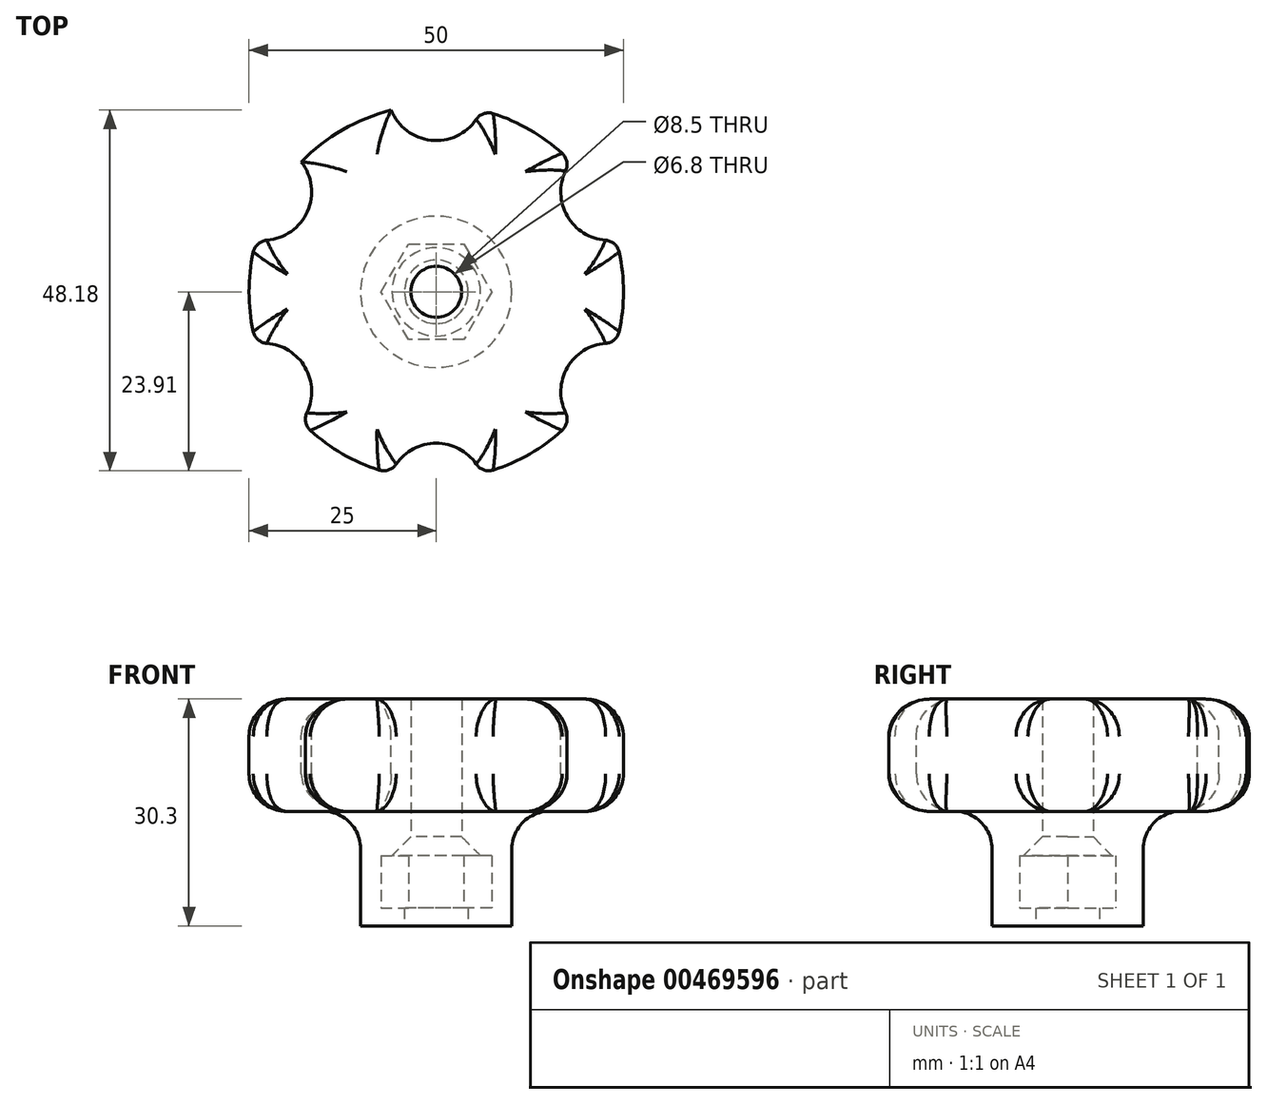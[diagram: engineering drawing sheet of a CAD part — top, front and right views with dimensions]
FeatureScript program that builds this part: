
annotation { "Feature Type Name" : "Feature", "Feature Type Description" : "" }
export const myFeature = defineFeature(function(context is Context, id is Id, definition is map)
    precondition{}
    {
        {
            var Q0;
            Q0=qCreatedBy(makeId("Top.planeOp"),FACE);
            var sketch = newSketch(context, id + "F0", { "sketchPlane" : qUnion([Q0])});
            skLineSegment(sketch, "E0.0", {"start": v(-7.4, 0) * mm, "end": v(-3.7, 6.4) * mm});
            skLineSegment(sketch, "E0.1", {"start": v(-3.7, 6.4) * mm, "end": v(3.7, 6.4) * mm});
            skLineSegment(sketch, "E0.2", {"start": v(3.7, 6.4) * mm, "end": v(7.4, 0) * mm});
            skLineSegment(sketch, "E0.3", {"start": v(7.4, 0) * mm, "end": v(3.7, -6.4) * mm});
            skLineSegment(sketch, "E0.4", {"start": v(3.7, -6.4) * mm, "end": v(-3.7, -6.4) * mm});
            skLineSegment(sketch, "E0.5", {"start": v(-3.7, -6.4) * mm, "end": v(-7.4, 0) * mm});
            skPoint(sketch, "E1.center.orphan", {"position": v(0, 0) * mm});
            skSolve(sketch);
        }
        {
            var Q0;
            Q0=makeQuery(id+"F0.imprint","IMPRINT",FACE,{"disambiguationData":[TD([[makeQuery(id+"F0.imprint","IMPRINT",EDGE,{"derivedFrom":sQuery(id+"F0.wireOp",EDGE,"E0.0")}),-1.0]])]});
            extrude(context, id + "F1", {"entities" : qUnion([Q0]), "depth" : 7 * mm});
        }
        {
            var Q0;
            Q0=qCreatedBy(makeId("Front.planeOp"),FACE);
            var sketch = newSketch(context, id + "F2", { "sketchPlane" : qUnion([Q0])});
            skLineSegment(sketch, "E2", {"start": v(-10.1, -2.4) * mm, "end": v(-10.1, 7.9) * mm});
            skLineSegment(sketch, "E3", {"start": v(-15.1, 12.9) * mm, "end": v(-25, 12.9) * mm});
            skLineSegment(sketch, "E4", {"start": v(-25, 12.9) * mm, "end": v(-25, 27.9) * mm});
            skLineSegment(sketch, "E5", {"start": v(-25, 27.9) * mm, "end": v(-3.4, 27.9) * mm});
            skLineSegment(sketch, "E6", {"start": v(-3.4, 27.9) * mm, "end": v(-3.4, 0) * mm});
            skLineSegment(sketch, "E7", {"start": v(-3.4, 0) * mm, "end": v(-4.25, 0) * mm});
            skLineSegment(sketch, "E8", {"start": v(-4.25, 0) * mm, "end": v(-4.25, -2.4) * mm});
            skLineSegment(sketch, "E9", {"start": v(-4.25, -2.4) * mm, "end": v(-10.1, -2.4) * mm});
            skLineSegment(sketch, "E10", {"start": v(0, 0) * mm, "end": v(0, 19.48) * mm});
            skPoint(sketch, "E11.visualSharp", {"position": v(-10.1, 12.9) * mm});
            skArc(sketch, "E11.filletArc", {"start": v(-10.1, 7.9) * mm, "mid": v(-11.56, 11.44) * mm, "end": v(-15.1, 12.9) * mm});
            skSolve(sketch);
        }
        {
            var Q0;
            Q0=makeQuery(id+"F2.imprint","IMPRINT",FACE,{"disambiguationData":[TD([[makeQuery(id+"F2.imprint","IMPRINT",EDGE,{"derivedFrom":sQuery(id+"F2.wireOp",EDGE,"E2")}),-1.0]])]});
            var Q1;
            Q1=sQuery(id+"F2.wireOp",EDGE,"E10");
            revolve(context, id + "F3", {"entities" : qUnion([Q0]), "axis" : qUnion([Q1]), "revolveType" : RevolveType.FULL});
        }
        {
            var Q0;
            Q0=makeQuery(id+"F3.opRevolve","SWEPT_FACE",FACE,{"disambiguationData":[OSD([sQuery(id+"F2.wireOp",EDGE,"E5")])]});
            var sketch = newSketch(context, id + "F4", { "sketchPlane" : qUnion([Q0])});
            skPoint(sketch, "E12.cCircle.center.orphan", {"position": v(0, 0) * mm});
            skArc(sketch, "E13", {"start": v(-24.02, 6.93) * mm, "mid": v(-25, 0) * mm, "end": v(-24.02, -6.93) * mm});
            skArc(sketch, "E14", {"start": v(-24.02, 6.93) * mm, "mid": v(-17.5, 10.1) * mm, "end": v(-18.01, 17.34) * mm});
            skArc(sketch, "E15", {"start": v(-6, 24.27) * mm, "mid": v(0, 20.21) * mm, "end": v(6, 24.27) * mm});
            skArc(sketch, "E16", {"start": v(18.01, 17.34) * mm, "mid": v(17.5, 10.1) * mm, "end": v(24.02, 6.93) * mm});
            skArc(sketch, "E17", {"start": v(24.02, -6.93) * mm, "mid": v(17.5, -10.1) * mm, "end": v(18.01, -17.34) * mm});
            skArc(sketch, "E18", {"start": v(6, -24.27) * mm, "mid": v(0, -20.21) * mm, "end": v(-6, -24.27) * mm});
            skArc(sketch, "E19", {"start": v(-18.01, -17.34) * mm, "mid": v(-17.5, -10.1) * mm, "end": v(-24.02, -6.93) * mm});
            skArc(sketch, "E20.trimOffspring", {"start": v(-6, 24.27) * mm, "mid": v(-12.5, 21.65) * mm, "end": v(-18.01, 17.34) * mm});
            skArc(sketch, "E21.trimOffspring", {"start": v(18.01, 17.34) * mm, "mid": v(12.5, 21.65) * mm, "end": v(6, 24.27) * mm});
            skArc(sketch, "E22.trimOffspring", {"start": v(6, -24.27) * mm, "mid": v(12.5, -21.65) * mm, "end": v(18.01, -17.34) * mm});
            skArc(sketch, "E23.trimOffspring", {"start": v(24.02, -6.93) * mm, "mid": v(25, 0) * mm, "end": v(24.02, 6.93) * mm});
            skPoint(sketch, "E24.start.orphan", {"position": v(-25, 0) * mm});
            skArc(sketch, "E25.trimOffspring", {"start": v(-18.01, -17.34) * mm, "mid": v(-12.5, -21.65) * mm, "end": v(-6, -24.27) * mm});
            skSolve(sketch);
        }
        {
            var Q0;
            Q0 = qSketchRegion(id + "F4", true);
            extrude(context, id + "F5", {"entities" : qUnion([Q0]), "endBound" : BoundingType.SYMMETRIC, "oppositeDirection" : true, "depth" : 86.2 * mm});
        }
        {
            var Q0;
            Q0=makeQuery(id+"F3.opRevolve","SWEPT_BODY",BODY,{"disambiguationData":[OSD([sQuery(id+"F2.wireOp",EDGE,"E2"),sQuery(id+"F2.wireOp",EDGE,"E3"),sQuery(id+"F2.wireOp",EDGE,"E4"),sQuery(id+"F2.wireOp",EDGE,"E5"),sQuery(id+"F2.wireOp",EDGE,"E6"),sQuery(id+"F2.wireOp",EDGE,"E7"),sQuery(id+"F2.wireOp",EDGE,"E8"),sQuery(id+"F2.wireOp",EDGE,"E9")])]});
            var Q1;
            Q1=makeQuery(id+"F5.opExtrude","SWEPT_BODY",BODY,{"disambiguationData":[OSD([sQuery(id+"F4.wireOp",EDGE,"E13"),sQuery(id+"F4.wireOp",EDGE,"E14"),sQuery(id+"F4.wireOp",EDGE,"E15"),sQuery(id+"F4.wireOp",EDGE,"E16"),sQuery(id+"F4.wireOp",EDGE,"E17"),sQuery(id+"F4.wireOp",EDGE,"E18"),sQuery(id+"F4.wireOp",EDGE,"E19"),sQuery(id+"F4.wireOp",EDGE,"E20.trimOffspring"),sQuery(id+"F4.wireOp",EDGE,"E21.trimOffspring"),sQuery(id+"F4.wireOp",EDGE,"E22.trimOffspring"),sQuery(id+"F4.wireOp",EDGE,"E23.trimOffspring"),sQuery(id+"F4.wireOp",EDGE,"E25.trimOffspring")])]});
            booleanBodies(context, id + "F6", {"operationType" : BooleanOperationType.INTERSECTION, "tools" : qUnion([Q0, Q1])});
        }
        {
            var Q0;
            Q0=makeQuery(id+"F6.opBoolean","INTERSECT",EDGE,{"derivedFrom":[makeQuery(id+"F3.opRevolve","SWEPT_FACE",FACE,{"disambiguationData":[OSD([sQuery(id+"F2.wireOp",EDGE,"E5")])]}),makeQuery(id+"F5.opExtrude","SWEPT_FACE",FACE,{"disambiguationData":[OSD([sQuery(id+"F4.wireOp",EDGE,"E16")])]})]});
            var Q1;
            {var subQ0=sQuery(id+"F2.wireOp",EDGE,"E4");var subQ1=sQuery(id+"F2.wireOp",EDGE,"E5");Q1=makeQuery(id+"F6.opBoolean","SPLIT",EDGE,{"disambiguationData":[TD([makeQuery(id+"F3.opRevolve","SWEPT_FACE",FACE,{"disambiguationData":[OSD([subQ0])]}),makeQuery(id+"F3.opRevolve","SWEPT_FACE",FACE,{"disambiguationData":[OSD([subQ1])]}),makeQuery(id+"F5.opExtrude","SWEPT_FACE",FACE,{"disambiguationData":[OSD([sQuery(id+"F4.wireOp",EDGE,"E15")])]}),makeQuery(id+"F5.opExtrude","SWEPT_FACE",FACE,{"disambiguationData":[OSD([sQuery(id+"F4.wireOp",EDGE,"E16")])]})])],"derivedFrom":makeQuery(id+"F3.opRevolve","SWEPT_EDGE",EDGE,{"disambiguationData":[OSD([subQ0,subQ1])]})});}
            var Q2;
            Q2=makeQuery(id+"F6.opBoolean","INTERSECT",EDGE,{"derivedFrom":[makeQuery(id+"F3.opRevolve","SWEPT_FACE",FACE,{"disambiguationData":[OSD([sQuery(id+"F2.wireOp",EDGE,"E5")])]}),makeQuery(id+"F5.opExtrude","SWEPT_FACE",FACE,{"disambiguationData":[OSD([sQuery(id+"F4.wireOp",EDGE,"E15")])]})]});
            var Q3;
            Q3=makeQuery(id+"F6.opBoolean","INTERSECT",EDGE,{"derivedFrom":[makeQuery(id+"F3.opRevolve","SWEPT_FACE",FACE,{"disambiguationData":[OSD([sQuery(id+"F2.wireOp",EDGE,"E5")])]}),makeQuery(id+"F5.opExtrude","SWEPT_FACE",FACE,{"disambiguationData":[OSD([sQuery(id+"F4.wireOp",EDGE,"E17")])]})]});
            var Q4;
            {var subQ0=sQuery(id+"F2.wireOp",EDGE,"E4");var subQ1=sQuery(id+"F2.wireOp",EDGE,"E5");Q4=makeQuery(id+"F6.opBoolean","SPLIT",EDGE,{"disambiguationData":[TD([makeQuery(id+"F3.opRevolve","SWEPT_FACE",FACE,{"disambiguationData":[OSD([subQ0])]}),makeQuery(id+"F3.opRevolve","SWEPT_FACE",FACE,{"disambiguationData":[OSD([subQ1])]}),makeQuery(id+"F5.opExtrude","SWEPT_FACE",FACE,{"disambiguationData":[OSD([sQuery(id+"F4.wireOp",EDGE,"E16")])]}),makeQuery(id+"F5.opExtrude","SWEPT_FACE",FACE,{"disambiguationData":[OSD([sQuery(id+"F4.wireOp",EDGE,"E17")])]})])],"derivedFrom":makeQuery(id+"F3.opRevolve","SWEPT_EDGE",EDGE,{"disambiguationData":[OSD([subQ0,subQ1])]})});}
            var Q5;
            Q5=makeQuery(id+"F6.opBoolean","INTERSECT",EDGE,{"derivedFrom":[makeQuery(id+"F3.opRevolve","SWEPT_FACE",FACE,{"disambiguationData":[OSD([sQuery(id+"F2.wireOp",EDGE,"E5")])]}),makeQuery(id+"F5.opExtrude","SWEPT_FACE",FACE,{"disambiguationData":[OSD([sQuery(id+"F4.wireOp",EDGE,"E14")])]})]});
            var Q6;
            Q6=makeQuery(id+"F6.opBoolean","INTERSECT",EDGE,{"derivedFrom":[makeQuery(id+"F3.opRevolve","SWEPT_FACE",FACE,{"disambiguationData":[OSD([sQuery(id+"F2.wireOp",EDGE,"E5")])]}),makeQuery(id+"F5.opExtrude","SWEPT_FACE",FACE,{"disambiguationData":[OSD([sQuery(id+"F4.wireOp",EDGE,"E19")])]})]});
            var Q7;
            {var subQ0=sQuery(id+"F2.wireOp",EDGE,"E4");var subQ1=sQuery(id+"F2.wireOp",EDGE,"E5");Q7=makeQuery(id+"F6.opBoolean","SPLIT",EDGE,{"disambiguationData":[TD([makeQuery(id+"F3.opRevolve","SWEPT_FACE",FACE,{"disambiguationData":[OSD([subQ0])]}),makeQuery(id+"F3.opRevolve","SWEPT_FACE",FACE,{"disambiguationData":[OSD([subQ1])]}),makeQuery(id+"F5.opExtrude","SWEPT_FACE",FACE,{"disambiguationData":[OSD([sQuery(id+"F4.wireOp",EDGE,"E14")])]}),makeQuery(id+"F5.opExtrude","SWEPT_FACE",FACE,{"disambiguationData":[OSD([sQuery(id+"F4.wireOp",EDGE,"E19")])]})])],"derivedFrom":makeQuery(id+"F3.opRevolve","SWEPT_EDGE",EDGE,{"disambiguationData":[OSD([subQ0,subQ1])]})});}
            var Q8;
            {var subQ0=sQuery(id+"F2.wireOp",EDGE,"E4");var subQ1=sQuery(id+"F2.wireOp",EDGE,"E5");Q8=makeQuery(id+"F6.opBoolean","SPLIT",EDGE,{"disambiguationData":[TD([makeQuery(id+"F3.opRevolve","SWEPT_FACE",FACE,{"disambiguationData":[OSD([subQ0])]}),makeQuery(id+"F3.opRevolve","SWEPT_FACE",FACE,{"disambiguationData":[OSD([subQ1])]}),makeQuery(id+"F5.opExtrude","SWEPT_FACE",FACE,{"disambiguationData":[OSD([sQuery(id+"F4.wireOp",EDGE,"E14")])]}),makeQuery(id+"F5.opExtrude","SWEPT_FACE",FACE,{"disambiguationData":[OSD([sQuery(id+"F4.wireOp",EDGE,"E15")])]})])],"derivedFrom":makeQuery(id+"F3.opRevolve","SWEPT_EDGE",EDGE,{"disambiguationData":[OSD([subQ0,subQ1])]})});}
            var Q9;
            Q9=makeQuery(id+"F6.opBoolean","INTERSECT",EDGE,{"derivedFrom":[makeQuery(id+"F3.opRevolve","SWEPT_FACE",FACE,{"disambiguationData":[OSD([sQuery(id+"F2.wireOp",EDGE,"E5")])]}),makeQuery(id+"F5.opExtrude","SWEPT_FACE",FACE,{"disambiguationData":[OSD([sQuery(id+"F4.wireOp",EDGE,"E18")])]})]});
            var Q10;
            {var subQ0=sQuery(id+"F2.wireOp",EDGE,"E4");var subQ1=sQuery(id+"F2.wireOp",EDGE,"E5");Q10=makeQuery(id+"F6.opBoolean","SPLIT",EDGE,{"disambiguationData":[TD([makeQuery(id+"F3.opRevolve","SWEPT_FACE",FACE,{"disambiguationData":[OSD([subQ0])]}),makeQuery(id+"F3.opRevolve","SWEPT_FACE",FACE,{"disambiguationData":[OSD([subQ1])]}),makeQuery(id+"F5.opExtrude","SWEPT_FACE",FACE,{"disambiguationData":[OSD([sQuery(id+"F4.wireOp",EDGE,"E18")])]}),makeQuery(id+"F5.opExtrude","SWEPT_FACE",FACE,{"disambiguationData":[OSD([sQuery(id+"F4.wireOp",EDGE,"E19")])]})])],"derivedFrom":makeQuery(id+"F3.opRevolve","SWEPT_EDGE",EDGE,{"disambiguationData":[OSD([subQ0,subQ1])]})});}
            var Q11;
            {var subQ0=sQuery(id+"F2.wireOp",EDGE,"E4");var subQ1=sQuery(id+"F2.wireOp",EDGE,"E5");Q11=makeQuery(id+"F6.opBoolean","SPLIT",EDGE,{"disambiguationData":[TD([makeQuery(id+"F3.opRevolve","SWEPT_FACE",FACE,{"disambiguationData":[OSD([subQ0])]}),makeQuery(id+"F3.opRevolve","SWEPT_FACE",FACE,{"disambiguationData":[OSD([subQ1])]}),makeQuery(id+"F5.opExtrude","SWEPT_FACE",FACE,{"disambiguationData":[OSD([sQuery(id+"F4.wireOp",EDGE,"E17")])]}),makeQuery(id+"F5.opExtrude","SWEPT_FACE",FACE,{"disambiguationData":[OSD([sQuery(id+"F4.wireOp",EDGE,"E18")])]})])],"derivedFrom":makeQuery(id+"F3.opRevolve","SWEPT_EDGE",EDGE,{"disambiguationData":[OSD([subQ0,subQ1])]})});}
            fillet(context, id + "F7", {"entities" : qUnion([Q0, Q1, Q2, Q3, Q4, Q5, Q6, Q7, Q8, Q9, Q10, Q11]), "radius" : 5 * mm, "tangentPropagation" : true, "allowEdgeOverflow" : false});
        }
        {
            var Q0;
            Q0=makeQuery(id+"F6.opBoolean","INTERSECT",EDGE,{"derivedFrom":[makeQuery(id+"F3.opRevolve","SWEPT_FACE",FACE,{"disambiguationData":[OSD([sQuery(id+"F2.wireOp",EDGE,"E3")])]}),makeQuery(id+"F5.opExtrude","SWEPT_FACE",FACE,{"disambiguationData":[OSD([sQuery(id+"F4.wireOp",EDGE,"E18")])]})]});
            var Q1;
            Q1=makeQuery(id+"F6.opBoolean","INTERSECT",EDGE,{"derivedFrom":[makeQuery(id+"F3.opRevolve","SWEPT_FACE",FACE,{"disambiguationData":[OSD([sQuery(id+"F2.wireOp",EDGE,"E3")])]}),makeQuery(id+"F5.opExtrude","SWEPT_FACE",FACE,{"disambiguationData":[OSD([sQuery(id+"F4.wireOp",EDGE,"E17")])]})]});
            var Q2;
            Q2=makeQuery(id+"F6.opBoolean","INTERSECT",EDGE,{"derivedFrom":[makeQuery(id+"F3.opRevolve","SWEPT_FACE",FACE,{"disambiguationData":[OSD([sQuery(id+"F2.wireOp",EDGE,"E3")])]}),makeQuery(id+"F5.opExtrude","SWEPT_FACE",FACE,{"disambiguationData":[OSD([sQuery(id+"F4.wireOp",EDGE,"E19")])]})]});
            var Q3;
            {var subQ0=sQuery(id+"F2.wireOp",EDGE,"E3");var subQ1=sQuery(id+"F2.wireOp",EDGE,"E4");Q3=makeQuery(id+"F6.opBoolean","SPLIT",EDGE,{"disambiguationData":[TD([makeQuery(id+"F3.opRevolve","SWEPT_FACE",FACE,{"disambiguationData":[OSD([subQ0])]}),makeQuery(id+"F3.opRevolve","SWEPT_FACE",FACE,{"disambiguationData":[OSD([subQ1])]}),makeQuery(id+"F5.opExtrude","SWEPT_FACE",FACE,{"disambiguationData":[OSD([sQuery(id+"F4.wireOp",EDGE,"E18")])]}),makeQuery(id+"F5.opExtrude","SWEPT_FACE",FACE,{"disambiguationData":[OSD([sQuery(id+"F4.wireOp",EDGE,"E19")])]})])],"derivedFrom":makeQuery(id+"F3.opRevolve","SWEPT_EDGE",EDGE,{"disambiguationData":[OSD([subQ0,subQ1])]})});}
            var Q4;
            {var subQ0=sQuery(id+"F2.wireOp",EDGE,"E3");var subQ1=sQuery(id+"F2.wireOp",EDGE,"E4");Q4=makeQuery(id+"F6.opBoolean","SPLIT",EDGE,{"disambiguationData":[TD([makeQuery(id+"F3.opRevolve","SWEPT_FACE",FACE,{"disambiguationData":[OSD([subQ0])]}),makeQuery(id+"F3.opRevolve","SWEPT_FACE",FACE,{"disambiguationData":[OSD([subQ1])]}),makeQuery(id+"F5.opExtrude","SWEPT_FACE",FACE,{"disambiguationData":[OSD([sQuery(id+"F4.wireOp",EDGE,"E17")])]}),makeQuery(id+"F5.opExtrude","SWEPT_FACE",FACE,{"disambiguationData":[OSD([sQuery(id+"F4.wireOp",EDGE,"E18")])]})])],"derivedFrom":makeQuery(id+"F3.opRevolve","SWEPT_EDGE",EDGE,{"disambiguationData":[OSD([subQ0,subQ1])]})});}
            var Q5;
            Q5=makeQuery(id+"F6.opBoolean","INTERSECT",EDGE,{"derivedFrom":[makeQuery(id+"F3.opRevolve","SWEPT_FACE",FACE,{"disambiguationData":[OSD([sQuery(id+"F2.wireOp",EDGE,"E3")])]}),makeQuery(id+"F5.opExtrude","SWEPT_FACE",FACE,{"disambiguationData":[OSD([sQuery(id+"F4.wireOp",EDGE,"E16")])]})]});
            var Q6;
            Q6=makeQuery(id+"F6.opBoolean","INTERSECT",EDGE,{"derivedFrom":[makeQuery(id+"F3.opRevolve","SWEPT_FACE",FACE,{"disambiguationData":[OSD([sQuery(id+"F2.wireOp",EDGE,"E3")])]}),makeQuery(id+"F5.opExtrude","SWEPT_FACE",FACE,{"disambiguationData":[OSD([sQuery(id+"F4.wireOp",EDGE,"E15")])]})]});
            var Q7;
            Q7=makeQuery(id+"F6.opBoolean","INTERSECT",EDGE,{"derivedFrom":[makeQuery(id+"F3.opRevolve","SWEPT_FACE",FACE,{"disambiguationData":[OSD([sQuery(id+"F2.wireOp",EDGE,"E3")])]}),makeQuery(id+"F5.opExtrude","SWEPT_FACE",FACE,{"disambiguationData":[OSD([sQuery(id+"F4.wireOp",EDGE,"E14")])]})]});
            var Q8;
            {var subQ0=sQuery(id+"F2.wireOp",EDGE,"E3");var subQ1=sQuery(id+"F2.wireOp",EDGE,"E4");Q8=makeQuery(id+"F6.opBoolean","SPLIT",EDGE,{"disambiguationData":[TD([makeQuery(id+"F3.opRevolve","SWEPT_FACE",FACE,{"disambiguationData":[OSD([subQ0])]}),makeQuery(id+"F3.opRevolve","SWEPT_FACE",FACE,{"disambiguationData":[OSD([subQ1])]}),makeQuery(id+"F5.opExtrude","SWEPT_FACE",FACE,{"disambiguationData":[OSD([sQuery(id+"F4.wireOp",EDGE,"E16")])]}),makeQuery(id+"F5.opExtrude","SWEPT_FACE",FACE,{"disambiguationData":[OSD([sQuery(id+"F4.wireOp",EDGE,"E17")])]})])],"derivedFrom":makeQuery(id+"F3.opRevolve","SWEPT_EDGE",EDGE,{"disambiguationData":[OSD([subQ0,subQ1])]})});}
            var Q9;
            {var subQ0=sQuery(id+"F2.wireOp",EDGE,"E3");var subQ1=sQuery(id+"F2.wireOp",EDGE,"E4");Q9=makeQuery(id+"F6.opBoolean","SPLIT",EDGE,{"disambiguationData":[TD([makeQuery(id+"F3.opRevolve","SWEPT_FACE",FACE,{"disambiguationData":[OSD([subQ0])]}),makeQuery(id+"F3.opRevolve","SWEPT_FACE",FACE,{"disambiguationData":[OSD([subQ1])]}),makeQuery(id+"F5.opExtrude","SWEPT_FACE",FACE,{"disambiguationData":[OSD([sQuery(id+"F4.wireOp",EDGE,"E15")])]}),makeQuery(id+"F5.opExtrude","SWEPT_FACE",FACE,{"disambiguationData":[OSD([sQuery(id+"F4.wireOp",EDGE,"E16")])]})])],"derivedFrom":makeQuery(id+"F3.opRevolve","SWEPT_EDGE",EDGE,{"disambiguationData":[OSD([subQ0,subQ1])]})});}
            var Q10;
            {var subQ0=sQuery(id+"F2.wireOp",EDGE,"E3");var subQ1=sQuery(id+"F2.wireOp",EDGE,"E4");Q10=makeQuery(id+"F6.opBoolean","SPLIT",EDGE,{"disambiguationData":[TD([makeQuery(id+"F3.opRevolve","SWEPT_FACE",FACE,{"disambiguationData":[OSD([subQ0])]}),makeQuery(id+"F3.opRevolve","SWEPT_FACE",FACE,{"disambiguationData":[OSD([subQ1])]}),makeQuery(id+"F5.opExtrude","SWEPT_FACE",FACE,{"disambiguationData":[OSD([sQuery(id+"F4.wireOp",EDGE,"E14")])]}),makeQuery(id+"F5.opExtrude","SWEPT_FACE",FACE,{"disambiguationData":[OSD([sQuery(id+"F4.wireOp",EDGE,"E15")])]})])],"derivedFrom":makeQuery(id+"F3.opRevolve","SWEPT_EDGE",EDGE,{"disambiguationData":[OSD([subQ0,subQ1])]})});}
            var Q11;
            {var subQ0=sQuery(id+"F2.wireOp",EDGE,"E3");var subQ1=sQuery(id+"F2.wireOp",EDGE,"E4");Q11=makeQuery(id+"F6.opBoolean","SPLIT",EDGE,{"disambiguationData":[TD([makeQuery(id+"F3.opRevolve","SWEPT_FACE",FACE,{"disambiguationData":[OSD([subQ0])]}),makeQuery(id+"F3.opRevolve","SWEPT_FACE",FACE,{"disambiguationData":[OSD([subQ1])]}),makeQuery(id+"F5.opExtrude","SWEPT_FACE",FACE,{"disambiguationData":[OSD([sQuery(id+"F4.wireOp",EDGE,"E14")])]}),makeQuery(id+"F5.opExtrude","SWEPT_FACE",FACE,{"disambiguationData":[OSD([sQuery(id+"F4.wireOp",EDGE,"E19")])]})])],"derivedFrom":makeQuery(id+"F3.opRevolve","SWEPT_EDGE",EDGE,{"disambiguationData":[OSD([subQ0,subQ1])]})});}
            fillet(context, id + "F8", {"entities" : qUnion([Q0, Q1, Q2, Q3, Q4, Q5, Q6, Q7, Q8, Q9, Q10, Q11]), "radius" : 5 * mm, "tangentPropagation" : true, "allowEdgeOverflow" : false});
        }
        {
            var Q0;
            Q0=makeQuery(id+"F5.opExtrude","SWEPT_EDGE",EDGE,{"disambiguationData":[OSD([sQuery(id+"F2.wireOp",EDGE,"E4"),sQuery(id+"F2.wireOp",EDGE,"E5"),sQuery(id+"F4.wireOp",EDGE,"E15"),sQuery(id+"F4.wireOp",EDGE,"E20.trimOffspring")])]});
            var Q1;
            Q1=makeQuery(id+"F5.opExtrude","SWEPT_EDGE",EDGE,{"disambiguationData":[OSD([sQuery(id+"F2.wireOp",EDGE,"E4"),sQuery(id+"F2.wireOp",EDGE,"E5"),sQuery(id+"F4.wireOp",EDGE,"E15"),sQuery(id+"F4.wireOp",EDGE,"E21.trimOffspring")])]});
            var Q2;
            Q2=makeQuery(id+"F5.opExtrude","SWEPT_EDGE",EDGE,{"disambiguationData":[OSD([sQuery(id+"F2.wireOp",EDGE,"E4"),sQuery(id+"F2.wireOp",EDGE,"E5"),sQuery(id+"F4.wireOp",EDGE,"E16"),sQuery(id+"F4.wireOp",EDGE,"E21.trimOffspring")])]});
            var Q3;
            Q3=makeQuery(id+"F5.opExtrude","SWEPT_EDGE",EDGE,{"disambiguationData":[OSD([sQuery(id+"F2.wireOp",EDGE,"E4"),sQuery(id+"F2.wireOp",EDGE,"E5"),sQuery(id+"F4.wireOp",EDGE,"E14"),sQuery(id+"F4.wireOp",EDGE,"E20.trimOffspring")])]});
            var Q4;
            Q4=makeQuery(id+"F5.opExtrude","SWEPT_EDGE",EDGE,{"disambiguationData":[OSD([sQuery(id+"F2.wireOp",EDGE,"E4"),sQuery(id+"F2.wireOp",EDGE,"E5"),sQuery(id+"F4.wireOp",EDGE,"E13"),sQuery(id+"F4.wireOp",EDGE,"E14")])]});
            var Q5;
            Q5=makeQuery(id+"F5.opExtrude","SWEPT_EDGE",EDGE,{"disambiguationData":[OSD([sQuery(id+"F2.wireOp",EDGE,"E4"),sQuery(id+"F2.wireOp",EDGE,"E5"),sQuery(id+"F4.wireOp",EDGE,"E16"),sQuery(id+"F4.wireOp",EDGE,"E23.trimOffspring")])]});
            var Q6;
            Q6=makeQuery(id+"F5.opExtrude","SWEPT_EDGE",EDGE,{"disambiguationData":[OSD([sQuery(id+"F2.wireOp",EDGE,"E4"),sQuery(id+"F2.wireOp",EDGE,"E5"),sQuery(id+"F4.wireOp",EDGE,"E17"),sQuery(id+"F4.wireOp",EDGE,"E23.trimOffspring")])]});
            var Q7;
            Q7=makeQuery(id+"F5.opExtrude","SWEPT_EDGE",EDGE,{"disambiguationData":[OSD([sQuery(id+"F2.wireOp",EDGE,"E4"),sQuery(id+"F2.wireOp",EDGE,"E5"),sQuery(id+"F4.wireOp",EDGE,"E17"),sQuery(id+"F4.wireOp",EDGE,"E22.trimOffspring")])]});
            var Q8;
            Q8=makeQuery(id+"F5.opExtrude","SWEPT_EDGE",EDGE,{"disambiguationData":[OSD([sQuery(id+"F2.wireOp",EDGE,"E4"),sQuery(id+"F2.wireOp",EDGE,"E5"),sQuery(id+"F4.wireOp",EDGE,"E18"),sQuery(id+"F4.wireOp",EDGE,"E22.trimOffspring")])]});
            var Q9;
            Q9=makeQuery(id+"F5.opExtrude","SWEPT_EDGE",EDGE,{"disambiguationData":[OSD([sQuery(id+"F2.wireOp",EDGE,"E4"),sQuery(id+"F2.wireOp",EDGE,"E5"),sQuery(id+"F4.wireOp",EDGE,"E18"),sQuery(id+"F4.wireOp",EDGE,"E25.trimOffspring")])]});
            var Q10;
            Q10=makeQuery(id+"F5.opExtrude","SWEPT_EDGE",EDGE,{"disambiguationData":[OSD([sQuery(id+"F2.wireOp",EDGE,"E4"),sQuery(id+"F2.wireOp",EDGE,"E5"),sQuery(id+"F4.wireOp",EDGE,"E19"),sQuery(id+"F4.wireOp",EDGE,"E25.trimOffspring")])]});
            var Q11;
            Q11=makeQuery(id+"F5.opExtrude","SWEPT_EDGE",EDGE,{"disambiguationData":[OSD([sQuery(id+"F2.wireOp",EDGE,"E4"),sQuery(id+"F2.wireOp",EDGE,"E5"),sQuery(id+"F4.wireOp",EDGE,"E13"),sQuery(id+"F4.wireOp",EDGE,"E19")])]});
            fillet(context, id + "F9", {"entities" : qUnion([Q0, Q1, Q2, Q3, Q4, Q5, Q6, Q7, Q8, Q9, Q10, Q11]), "radius" : 2 * mm, "tangentPropagation" : true, "allowEdgeOverflow" : false});
        }
        {
            var Q0;
            Q0=makeQuery(id+"F1.opExtrude","SWEPT_BODY",BODY,{"disambiguationData":[OSD([sQuery(id+"F0.wireOp",EDGE,"E0.0"),sQuery(id+"F0.wireOp",EDGE,"E0.1"),sQuery(id+"F0.wireOp",EDGE,"E0.2"),sQuery(id+"F0.wireOp",EDGE,"E0.3"),sQuery(id+"F0.wireOp",EDGE,"E0.4"),sQuery(id+"F0.wireOp",EDGE,"E0.5")])]});
            var Q1;
            Q1=makeQuery(id+"F6.opBoolean","INTERSECT",BODY,{"derivedFrom":[makeQuery(id+"F3.opRevolve","SWEPT_BODY",BODY,{"disambiguationData":[OSD([sQuery(id+"F2.wireOp",EDGE,"E2"),sQuery(id+"F2.wireOp",EDGE,"E3"),sQuery(id+"F2.wireOp",EDGE,"E4"),sQuery(id+"F2.wireOp",EDGE,"E5"),sQuery(id+"F2.wireOp",EDGE,"E6"),sQuery(id+"F2.wireOp",EDGE,"E7"),sQuery(id+"F2.wireOp",EDGE,"E8"),sQuery(id+"F2.wireOp",EDGE,"E9")])]}),makeQuery(id+"F5.opExtrude","SWEPT_BODY",BODY,{"disambiguationData":[OSD([sQuery(id+"F4.wireOp",EDGE,"E13"),sQuery(id+"F4.wireOp",EDGE,"E14"),sQuery(id+"F4.wireOp",EDGE,"E15"),sQuery(id+"F4.wireOp",EDGE,"E16"),sQuery(id+"F4.wireOp",EDGE,"E17"),sQuery(id+"F4.wireOp",EDGE,"E18"),sQuery(id+"F4.wireOp",EDGE,"E19"),sQuery(id+"F4.wireOp",EDGE,"E20.trimOffspring"),sQuery(id+"F4.wireOp",EDGE,"E21.trimOffspring"),sQuery(id+"F4.wireOp",EDGE,"E22.trimOffspring"),sQuery(id+"F4.wireOp",EDGE,"E23.trimOffspring"),sQuery(id+"F4.wireOp",EDGE,"E25.trimOffspring")])]})]});
            booleanBodies(context, id + "F10", {"operationType" : BooleanOperationType.SUBTRACTION, "tools" : qUnion([Q0]), "targets" : qUnion([Q1])});
        }
        {
            var Q0;
            Q0=makeQuery(id+"F10.opBoolean","INTERSECT",EDGE,{"derivedFrom":[makeQuery(id+"F1.opExtrude","CAP_FACE",FACE,{"disambiguationData":[OSD([sQuery(id+"F0.wireOp",EDGE,"E0.0"),sQuery(id+"F0.wireOp",EDGE,"E0.1"),sQuery(id+"F0.wireOp",EDGE,"E0.2"),sQuery(id+"F0.wireOp",EDGE,"E0.3"),sQuery(id+"F0.wireOp",EDGE,"E0.4"),sQuery(id+"F0.wireOp",EDGE,"E0.5")])],"isStart":false}),makeQuery(id+"F3.opRevolve","SWEPT_FACE",FACE,{"disambiguationData":[OSD([sQuery(id+"F2.wireOp",EDGE,"E6")])]})]});
            chamfer(context, id + "F11", {"entities" : qUnion([Q0]), "width" : 2.5 * mm, "tangentPropagation" : true});
        }
    });
